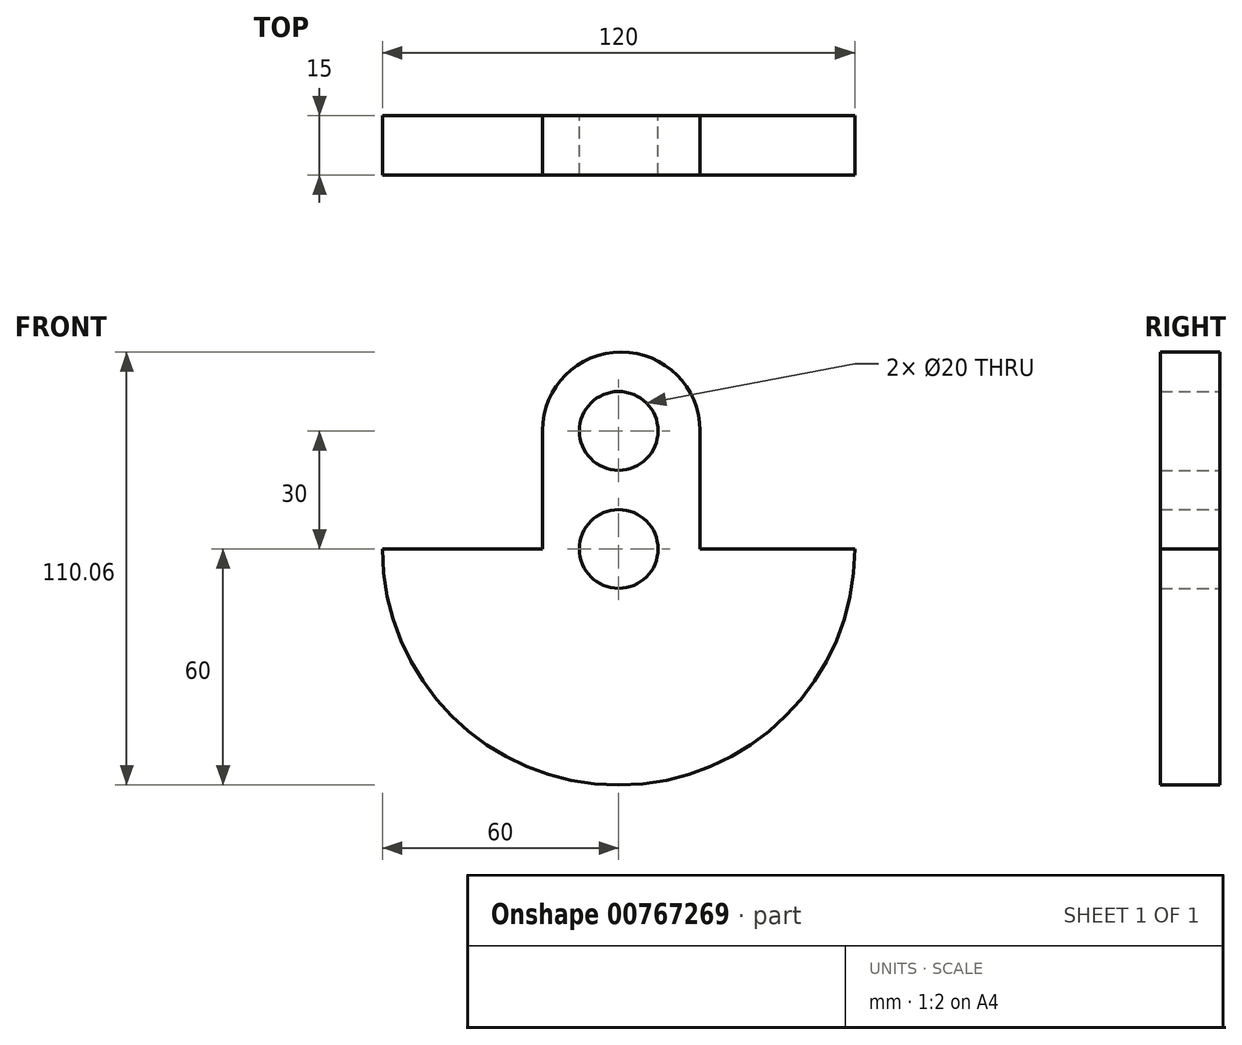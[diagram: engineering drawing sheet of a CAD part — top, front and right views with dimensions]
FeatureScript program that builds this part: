
annotation { "Feature Type Name" : "Feature", "Feature Type Description" : "" }
export const myFeature = defineFeature(function(context is Context, id is Id, definition is map)
    precondition{}
    {
        {
            var Q0;
            Q0=qCreatedBy(makeId("Front.planeOp"),FACE);
            var sketch = newSketch(context, id + "F0", { "sketchPlane" : qUnion([Q0])});
            skArc(sketch, "E0", {"start": v(-60, 0) * mm, "mid": v(0, -60) * mm, "end": v(60, 0) * mm});
            skCircle(sketch, "E1", {"center": v(0, 0) * mm, "radius": 10 * mm});
            skLineSegment(sketch, "E2", {"start": v(-60, 0) * mm, "end": v(60, 0) * mm});
            skCircle(sketch, "E3", {"center": v(0, 30) * mm, "radius": 10 * mm});
            skLineSegment(sketch, "E4", {"start": v(-19.36, 30.05) * mm, "end": v(20.64, 30.05) * mm});
            skArc(sketch, "E5", {"start": v(20.64, 30.05) * mm, "mid": v(0.64, 50.06) * mm, "end": v(-19.36, 30.05) * mm});
            skLineSegment(sketch, "E6", {"start": v(-19.36, 30.05) * mm, "end": v(-19.36, 0) * mm});
            skLineSegment(sketch, "E7", {"start": v(20.64, 30.05) * mm, "end": v(20.64, 0) * mm});
            skSolve(sketch);
        }
        {
            var Q0;
            {var subQ4=sQuery(id+"F0.wireOp",EDGE,"E0");Q0=makeQuery(id+"F0.imprint","IMPRINT",FACE,{"disambiguationData":[TD([[makeQuery(id+"F0.imprint","IMPRINT",EDGE,{"derivedFrom":subQ4}),1.0]])]});}
            var Q1;
            {var subQ4=sQuery(id+"F0.wireOp",EDGE,"E6");Q1=makeQuery(id+"F0.imprint","IMPRINT",FACE,{"disambiguationData":[TD([[makeQuery(id+"F0.imprint","IMPRINT",EDGE,{"derivedFrom":subQ4}),1.0]])]});}
            var Q2;
            {var subQ4=sQuery(id+"F0.wireOp",EDGE,"E5");Q2=makeQuery(id+"F0.imprint","IMPRINT",FACE,{"disambiguationData":[TD([[makeQuery(id+"F0.imprint","IMPRINT",EDGE,{"derivedFrom":subQ4}),1.0]])]});}
            extrude(context, id + "F1", {"entities" : qUnion([Q0, Q1, Q2]), "depth" : 15 * mm, "offsetDistance" : 25 * mm});
        }
    });
